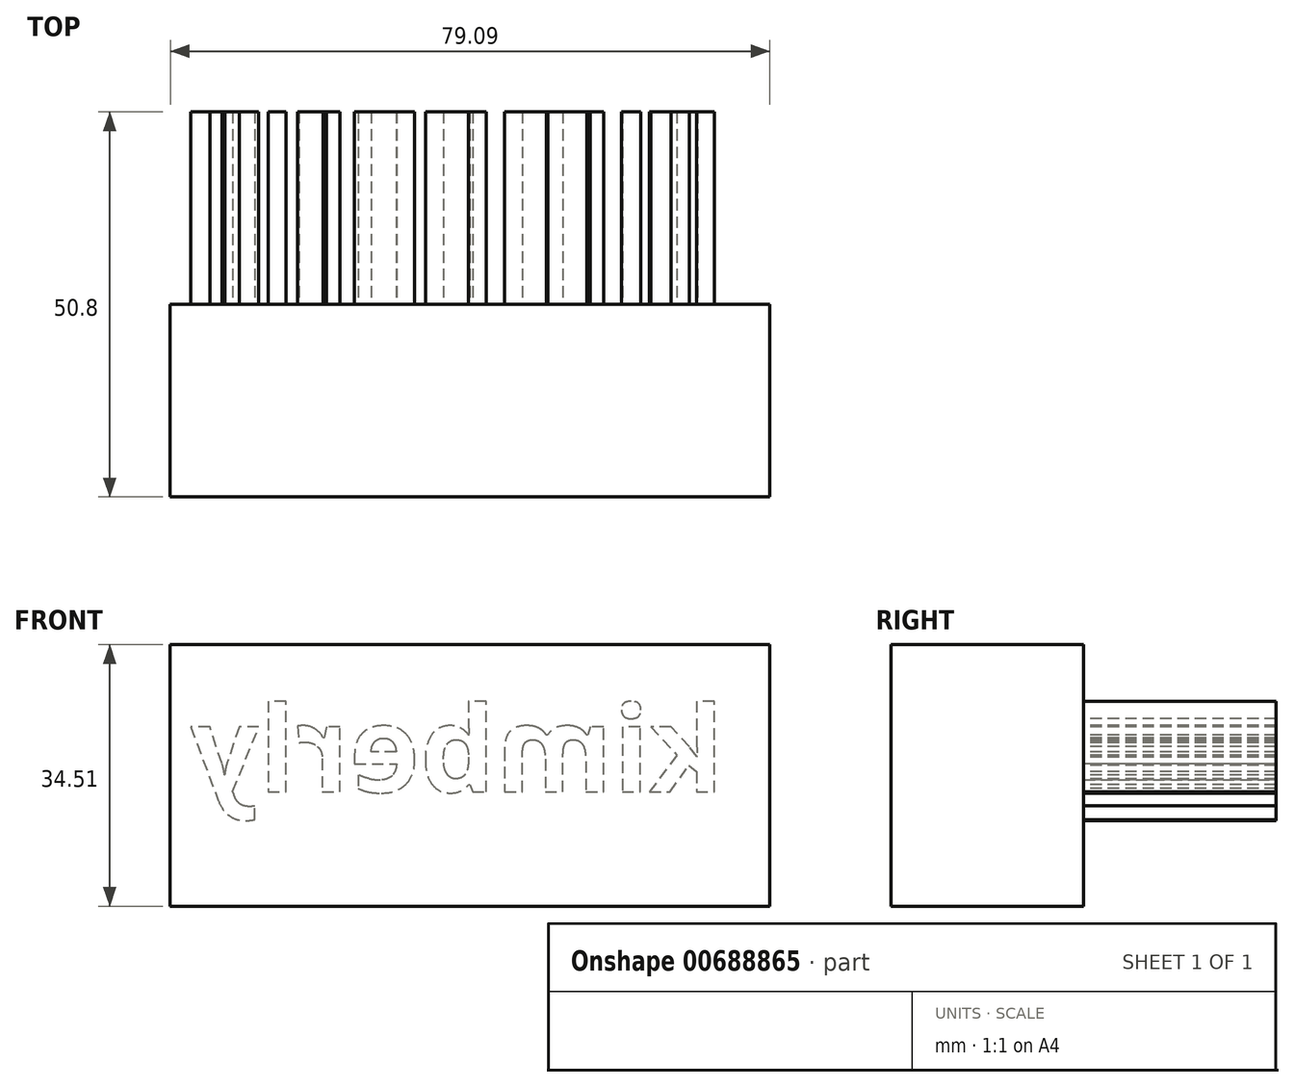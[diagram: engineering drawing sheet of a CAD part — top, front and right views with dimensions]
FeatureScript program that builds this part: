
annotation { "Feature Type Name" : "Feature", "Feature Type Description" : "" }
export const myFeature = defineFeature(function(context is Context, id is Id, definition is map)
    precondition{}
    {
        {
            var Q0;
            Q0=qCreatedBy(makeId("Front.planeOp"),FACE);
            var sketch = newSketch(context, id + "F0", { "sketchPlane" : qUnion([Q0])});
            skLineSegment(sketch, "E0.bottom", {"start": v(42.6, 44.13) * mm, "end": v(-36.5, 44.13) * mm});
            skLineSegment(sketch, "E0.top", {"start": v(42.6, 9.62) * mm, "end": v(-36.5, 9.62) * mm});
            skLineSegment(sketch, "E0.left", {"start": v(42.6, 44.13) * mm, "end": v(42.6, 9.62) * mm});
            skLineSegment(sketch, "E0.right", {"start": v(-36.5, 44.13) * mm, "end": v(-36.5, 9.62) * mm});
            skSolve(sketch);
        }
        {
            var Q0;
            Q0=makeQuery(id+"F0.imprint","IMPRINT",FACE,{"disambiguationData":[TD([[makeQuery(id+"F0.imprint","IMPRINT",EDGE,{"derivedFrom":sQuery(id+"F0.wireOp",EDGE,"E0.bottom")}),1.0]])]});
            extrude(context, id + "F1", {"entities" : qUnion([Q0]), "depth" : 25.4 * mm, "offsetDistance" : 25.4 * mm});
        }
        {
            var Q0;
            Q0=makeQuery(id+"F1.opExtrude","CAP_FACE",FACE,{"disambiguationData":[OSD([sQuery(id+"F0.wireOp",EDGE,"E0.bottom"),sQuery(id+"F0.wireOp",EDGE,"E0.top"),sQuery(id+"F0.wireOp",EDGE,"E0.left"),sQuery(id+"F0.wireOp",EDGE,"E0.right")])],"isStart":true});
            var sketch = newSketch(context, id + "F2", { "sketchPlane" : qUnion([Q0])});
            skText(sketch, "E1", { "text": "kimberly", "fontName": "OpenSans-Bold.ttf"});
            const initialGuessF2  = {"E1": [-0.0365, 0.0247, 1, 0, 0.01135]};
            skSetInitialGuess(sketch, initialGuessF2);
            skSolve(sketch);
        }
        {
            var Q0;
            Q0 = qSketchRegion(id + "F2", true);
            extrude(context, id + "F3", {"entities" : qUnion([Q0]), "operationType" : NewBodyOperationType.ADD, "depth" : 25.4 * mm, "offsetDistance" : 25.4 * mm});
        }
    });
